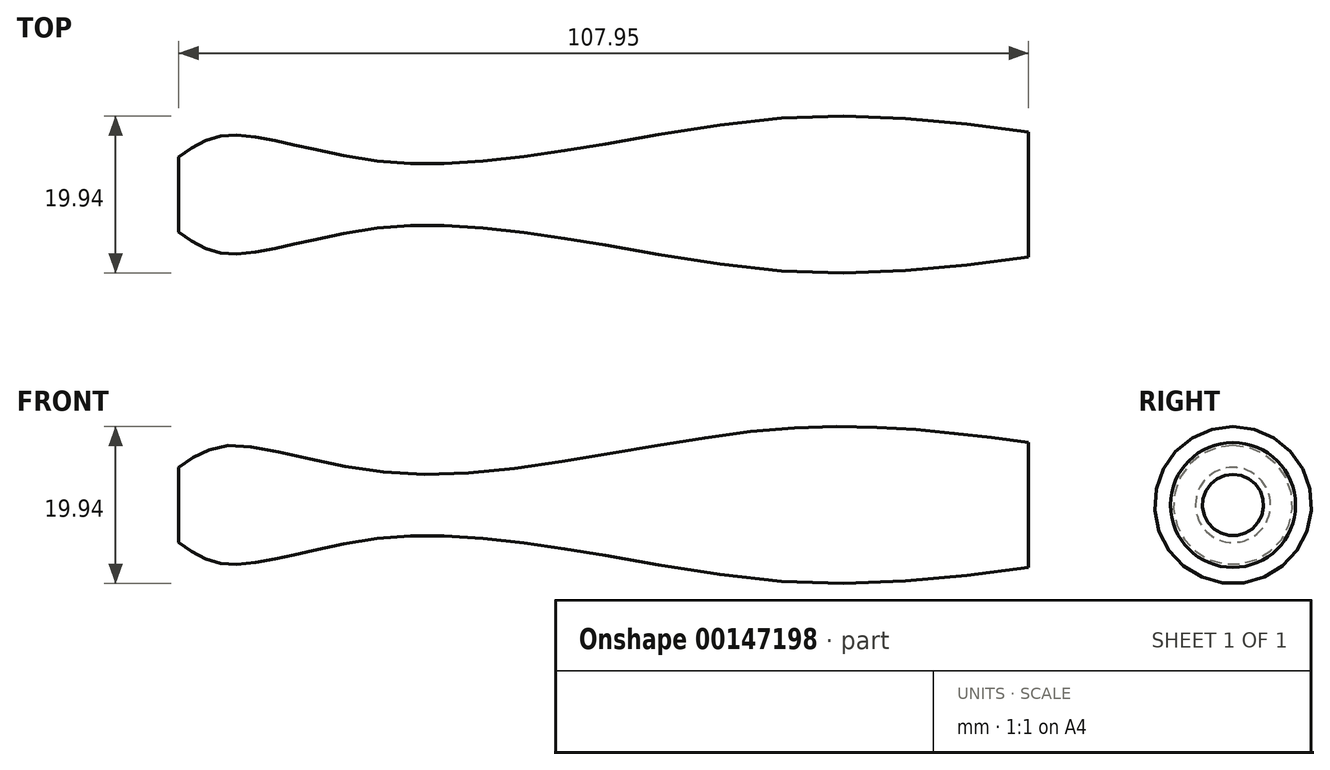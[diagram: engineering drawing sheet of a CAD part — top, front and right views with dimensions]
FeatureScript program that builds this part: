
annotation { "Feature Type Name" : "Feature", "Feature Type Description" : "" }
export const myFeature = defineFeature(function(context is Context, id is Id, definition is map)
    precondition{}
    {
        {
            var Q0;
            Q0=qCreatedBy(makeId("Front.planeOp"),FACE);
            var sketch = newSketch(context, id + "F0", { "sketchPlane" : qUnion([Q0])});
            skLineSegment(sketch, "E0", {"start": v(0, 0) * mm, "end": v(-107.95, 0) * mm});
            skLineSegment(sketch, "E1", {"start": v(0, 7.94) * mm, "end": v(0, 0) * mm});
            skLineSegment(sketch, "E2", {"start": v(-107.95, 0) * mm, "end": v(-107.95, 4.76) * mm});
            skLineSegment(sketch, "E3", {"start": v(-107.95, 0) * mm, "end": v(-101.6, 0) * mm});
            skLineSegment(sketch, "E4", {"start": v(-107.95, 0) * mm, "end": v(-79.38, 0) * mm});
            skLineSegment(sketch, "E5", {"start": v(0, 0) * mm, "end": v(-33.34, 0) * mm});
            skLineSegment(sketch, "E6", {"start": v(-33.34, 0) * mm, "end": v(-33.34, 9.52) * mm});
            skLineSegment(sketch, "E7", {"start": v(-79.38, 0) * mm, "end": v(-79.38, 3.97) * mm});
            skLineSegment(sketch, "E8", {"start": v(-101.6, 0) * mm, "end": v(-101.6, 7.54) * mm});
            skFitSpline(sketch, "E9", {"points": [v(-107.95, 4.76) * mm, v(-101.6, 7.54) * mm, v(-79.38, 3.97) * mm, v(-33.34, 9.53) * mm, v(0, 7.94) * mm], "startDerivative": vector(41.44, 29.6) * mm, "endDerivative": vector(108.12, -14.35) * mm});
            skSolve(sketch);
        }
        {
            var Q0;
            Q0 = qSketchRegion(id + "F0", true);
            var Q1;
            Q1 = qSketchRegion(id + "FdPYYGIxWw7OvK6_0", true);
            var Q2;
            Q2=sQuery(id+"F0.wireOp",EDGE,"E9");
            var Q3;
            Q3=sQuery(id+"F0.wireOp",EDGE,"E5");
            revolve(context, id + "F1", {"bodyType" : ToolBodyType.SURFACE, "entities" : qUnion([Q0, Q1]), "surfaceEntities" : qUnion([Q2]), "axis" : qUnion([Q3]), "revolveType" : RevolveType.FULL});
        }
    });
